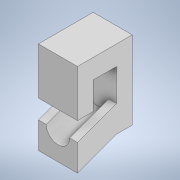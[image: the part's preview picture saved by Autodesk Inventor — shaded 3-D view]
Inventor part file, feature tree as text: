
AUTODESK INVENTOR PART (.ipt)
format: ipt  version: 2021 (Build 250183000, 183)  size: 158,720 bytes
history: native  units: mm
features: sketch x7, extrude x5, plane x1, sweep x1, thread x1
ambient origin geometry x8: Origin, YZ Plane, XZ Plane, XY Plane, X Axis, Y Axis, Z Axis, Center Point
bodies: Solid1 (feature_tree)
feature tree (15):
  extrude  "Extrusion1"  Depth=50.0mm
  extrude  "Extrusion2"  Depth=12.5mm
  extrude  "Extrusion3"  Depth=10.0mm
  extrude  "Extrusion4"  Depth=6.0mm TaperAngle=0.0deg
  extrude  "Extrusion5"  Depth=15.0mm TaperAngle=0.0deg
  sketch  "Sketch6"  dims[d14=25.0mm d15=10.0mm d16=0.0mm d17=15.0mm]
  plane  "Work Plane1"
  sweep  "Sweep1"
  thread  "Thread1"  [1 undecoded]
  sketch  "Sketch1"  dims[d0=25.0mm d1=50.0mm]
  sketch  "Sketch2"  dims[d2=12.5mm d3=12.5mm]
  sketch  "Sketch3"  dims[d4=10.0mm d5=0.0mm d7=3.0mm]
  sketch  "Sketch4"  dims[d8=33.0mm d9=6.0mm d10=0.0mm]
  sketch  "Sketch5"  dims[d11=15.0mm d12=15.0mm d13=0.0mm]
  sketch  "Sketch8"  dims[d18=15.0mm d19=10.0mm d20=0.0mm d21=30.0mm d22=15.0mm d23=17.0mm d24=17.0mm d25=-12.5mm d26=3.490659mm d27=8.5mm d28=0.0mm d29=0.0mm d30=6.0mm d31=0.0mm d32=25.0mm d33=0.872665mm d34=0.5mm d35=0.872665mm]
note: 1 required parameter value undecoded (feature->parameter linkage not recoverable at this tier; creation-order binding heuristic only, values carry confidence <= 0.55)
